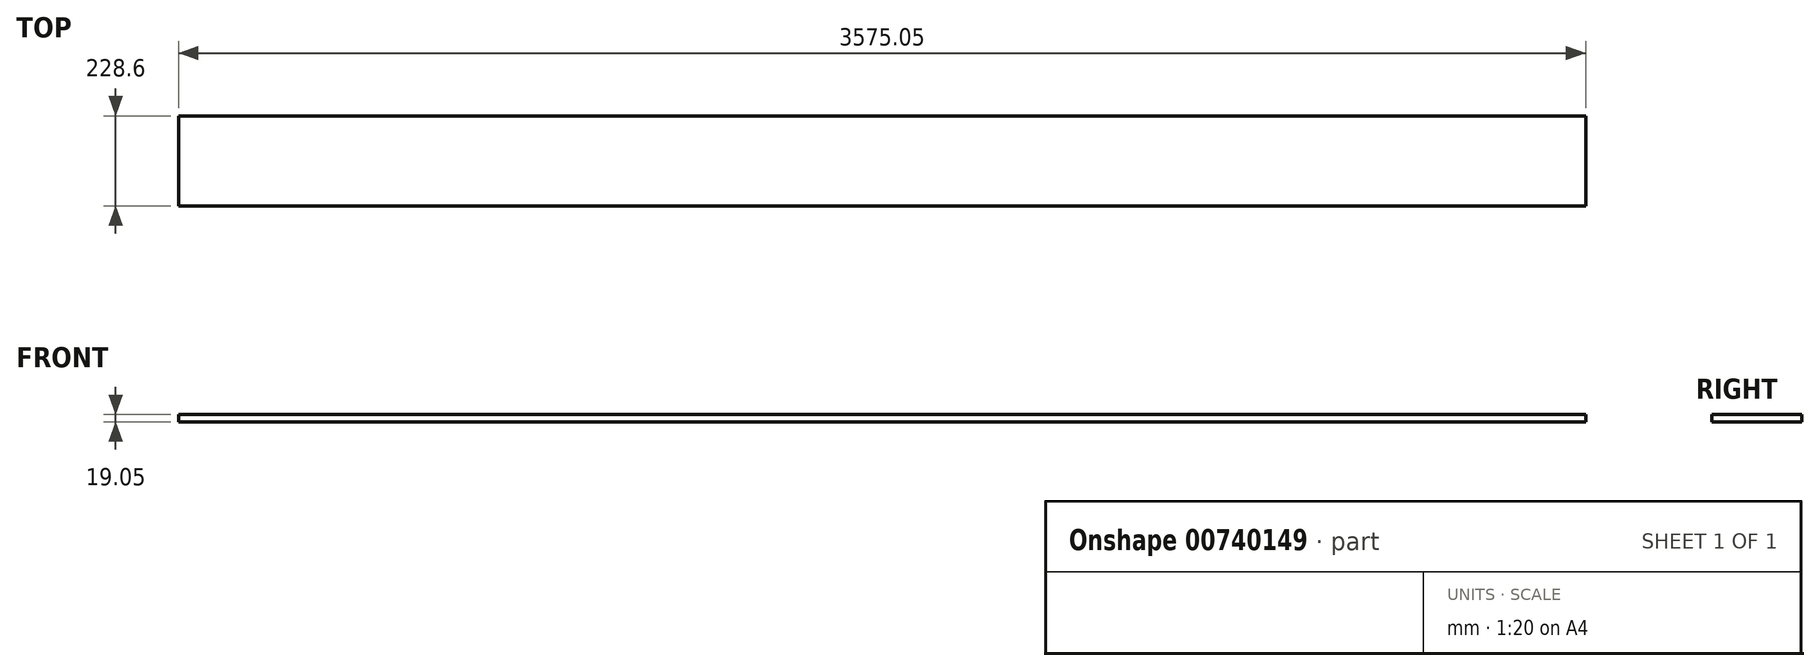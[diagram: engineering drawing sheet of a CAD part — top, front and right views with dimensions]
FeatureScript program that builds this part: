
annotation { "Feature Type Name" : "Feature", "Feature Type Description" : "" }
export const myFeature = defineFeature(function(context is Context, id is Id, definition is map)
    precondition{}
    {
        {
            var Q0;
            Q0=qCreatedBy(makeId("Top.planeOp"),FACE);
            var sketch = newSketch(context, id + "F0", { "sketchPlane" : qUnion([Q0])});
            skLineSegment(sketch, "E0.bottom", {"start": v(-897.52, -220.68) * mm, "end": v(2677.53, -220.68) * mm});
            skLineSegment(sketch, "E0.top", {"start": v(-897.52, -449.28) * mm, "end": v(2677.53, -449.28) * mm});
            skLineSegment(sketch, "E0.left", {"start": v(-897.52, -220.68) * mm, "end": v(-897.52, -449.28) * mm});
            skLineSegment(sketch, "E0.right", {"start": v(2677.53, -220.68) * mm, "end": v(2677.53, -449.28) * mm});
            skSolve(sketch);
        }
        {
            var Q0;
            Q0=makeQuery(id+"F0.imprint","IMPRINT",FACE,{"disambiguationData":[TD([[makeQuery(id+"F0.imprint","IMPRINT",EDGE,{"derivedFrom":sQuery(id+"F0.wireOp",EDGE,"E0.bottom")}),-1.0]])]});
            extrude(context, id + "F1", {"entities" : qUnion([Q0]), "depth" : 19.05 * mm, "offsetDistance" : 25.4 * mm});
        }
    });
